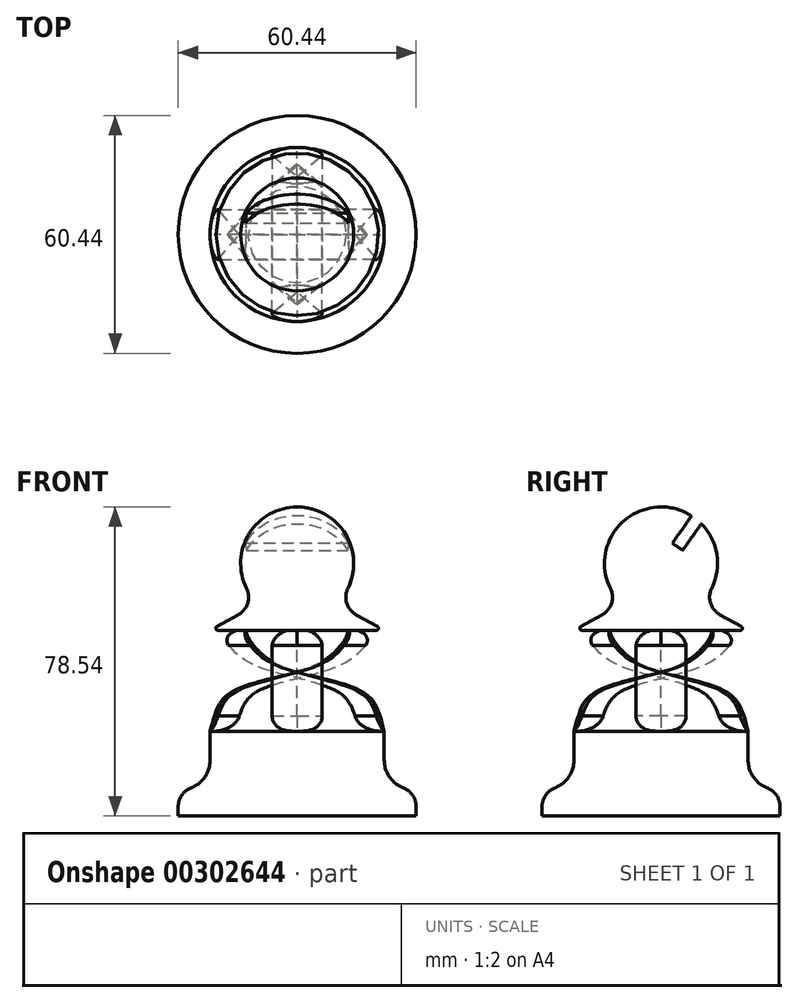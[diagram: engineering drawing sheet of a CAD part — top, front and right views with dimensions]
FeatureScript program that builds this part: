
annotation { "Feature Type Name" : "Feature", "Feature Type Description" : "" }
export const myFeature = defineFeature(function(context is Context, id is Id, definition is map)
    precondition{}
    {
        {
            var Q0;
            Q0=qCreatedBy(makeId("Front.planeOp"),FACE);
            var sketch = newSketch(context, id + "F0", { "sketchPlane" : qUnion([Q0])});
            skLineSegment(sketch, "E0", {"start": v(0, 0) * mm, "end": v(-30.22, 0) * mm});
            skLineSegment(sketch, "E1", {"start": v(-30.22, 0) * mm, "end": v(-30.22, 6.62) * mm});
            skLineSegment(sketch, "E2", {"start": v(-30.22, 6.62) * mm, "end": v(-22.11, 6.62) * mm});
            skLineSegment(sketch, "E3", {"start": v(-22.11, 6.62) * mm, "end": v(-22.11, 21.54) * mm});
            skLineSegment(sketch, "E4", {"start": v(-22.11, 21.54) * mm, "end": v(0, 21.54) * mm});
            skLineSegment(sketch, "E5", {"start": v(0, 21.54) * mm, "end": v(0, 0) * mm});
            skLineSegment(sketch, "E6", {"start": v(0, 47.18) * mm, "end": v(-22.11, 47.18) * mm});
            skLineSegment(sketch, "E7", {"start": v(-22.11, 47.18) * mm, "end": v(-10, 53.9) * mm});
            skArc(sketch, "E8", {"start": v(0, 78.54) * mm, "mid": v(-13.3, 69.58) * mm, "end": v(-10, 53.9) * mm});
            skLineSegment(sketch, "E9", {"start": v(0, 47.18) * mm, "end": v(0, 78.54) * mm});
            skSolve(sketch);
        }
        {
            var Q0;
            Q0=qSketchRegion(id+"F0",true);
            var Q1;
            Q1=sQuery(id+"F0.wireOp",EDGE,"E9");
            revolve(context, id + "F1", {"entities" : qUnion([Q0]), "axis" : qUnion([Q1]), "revolveType" : RevolveType.FULL});
        }
        {
            var Q0;
            Q0=makeQuery(id+"F1.opRevolve","SWEPT_FACE",FACE,{"disambiguationData":[OSD([sQuery(id+"F0.wireOp",EDGE,"E4")])]});
            var sketch = newSketch(context, id + "F2", { "sketchPlane" : qUnion([Q0])});
            skArc(sketch, "E10.0", {"start": v(-6.35, -21.18) * mm, "mid": v(0, -22.11) * mm, "end": v(6.35, -21.18) * mm});
            skLineSegment(sketch, "E11", {"start": v(-6.35, -21.18) * mm, "end": v(0, -15.76) * mm});
            skLineSegment(sketch, "E12", {"start": v(0, -15.76) * mm, "end": v(6.35, -21.18) * mm});
            skSolve(sketch);
        }
        {
            var Q0;
            Q0=makeQuery(id+"F1.opRevolve","SWEPT_EDGE",EDGE,{"disambiguationData":[OSD([sQuery(id+"F0.wireOp",EDGE,"E2"),sQuery(id+"F0.wireOp",EDGE,"E3")])]});
            fillet(context, id + "F3", {"entities" : qUnion([Q0]), "radius" : 7.62 * mm, "tangentPropagation" : true, "allowEdgeOverflow" : false});
        }
        {
            var Q0;
            Q0=makeQuery(id+"F1.opRevolve","SWEPT_EDGE",EDGE,{"disambiguationData":[OSD([sQuery(id+"F0.wireOp",EDGE,"E1"),sQuery(id+"F0.wireOp",EDGE,"E2")])]});
            fillet(context, id + "F4", {"entities" : qUnion([Q0]), "radius" : 5.08 * mm, "tangentPropagation" : true, "allowEdgeOverflow" : false});
        }
        {
            var Q0;
            Q0=makeQuery(id+"F1.opRevolve","SWEPT_EDGE",EDGE,{"disambiguationData":[OSD([sQuery(id+"F0.wireOp",EDGE,"E7"),sQuery(id+"F0.wireOp",EDGE,"E8")])]});
            fillet(context, id + "F5", {"entities" : qUnion([Q0]), "radius" : 5.08 * mm, "tangentPropagation" : true, "allowEdgeOverflow" : false});
        }
        {
            var Q0;
            Q0=qCreatedBy(makeId("Right.planeOp"),FACE);
            var sketch = newSketch(context, id + "F6", { "sketchPlane" : qUnion([Q0])});
            skFitSpline(sketch, "E13", {"points": [v(-15.76, 21.54) * mm, v(-12.86, 29.3) * mm, v(-7.35, 32.87) * mm, v(0, 35.04) * mm, v(6.19, 36.7) * mm, v(14.66, 40.62) * mm, v(19.27, 47.18) * mm], "startDerivative": vector(10.42, 41.06) * mm, "endDerivative": vector(-2.91, 25.6) * mm});
            skSolve(sketch);
        }
        {
            var Q0;
            Q0=makeQuery(id+"F2.imprint","IMPRINT",FACE,{"disambiguationData":[TD([[makeQuery(id+"F2.imprint","IMPRINT",EDGE,{"derivedFrom":sQuery(id+"F2.wireOp",EDGE,"E10.0")}),-1.0]])]});
            var Q1;
            Q1=sQuery(id+"F6.wireOp",EDGE,"E13");
            sweep(context, id + "F7", {"profiles" : qUnion([Q0]), "path" : qUnion([Q1]), "keepProfileOrientation" : true});
        }
        {
            var Q0;
            Q0=makeQuery(id+"F7.opSweep","SWEPT_BODY",BODY,{"disambiguationData":[OSD([sQuery(id+"F2.wireOp",EDGE,"E10.0"),sQuery(id+"F2.wireOp",EDGE,"E11"),sQuery(id+"F2.wireOp",EDGE,"E12"),sQuery(id+"F6.wireOp",EDGE,"E13")])]});
            var Q1;
            Q1=makeQuery(id+"F1.opRevolve","SWEPT_EDGE",EDGE,{"disambiguationData":[OSD([sQuery(id+"F0.wireOp",EDGE,"E3"),sQuery(id+"F0.wireOp",EDGE,"E4")])]});
            circularPattern(context, id + "F8", {"entities" : qUnion([Q0]), "axis" : qUnion([Q1]), "angle" : 360 * degree, "instanceCount" : 4, "equalSpace" : true});
        }
        {
            var Q0;
            Q0=makeQuery(id+"F1.opRevolve","SWEPT_EDGE",EDGE,{"disambiguationData":[OSD([sQuery(id+"F0.wireOp",EDGE,"E6"),sQuery(id+"F0.wireOp",EDGE,"E7")])]});
            fillet(context, id + "F9", {"entities" : qUnion([Q0]), "radius" : 0.5 * mm, "tangentPropagation" : true, "allowEdgeOverflow" : false});
        }
        {
            var Q0;
            Q0=makeQuery(id+"F8.opPattern","COPY",EDGE,{"derivedFrom":makeQuery(id+"F7.opSweep","CAP_EDGE",EDGE,{"disambiguationData":[OSD([sQuery(id+"F2.wireOp",EDGE,"E12"),sQuery(id+"F6.wireOp",VERTEX,"E13.start")])],"isStart":true}),"instanceName":"3"});
            var Q1;
            Q1=makeQuery(id+"F8.opPattern","COPY",EDGE,{"derivedFrom":makeQuery(id+"F7.opSweep","CAP_EDGE",EDGE,{"disambiguationData":[OSD([sQuery(id+"F2.wireOp",EDGE,"E11"),sQuery(id+"F6.wireOp",VERTEX,"E13.start")])],"isStart":true}),"instanceName":"2"});
            var Q2;
            Q2=makeQuery(id+"F8.opPattern","COPY",EDGE,{"derivedFrom":makeQuery(id+"F7.opSweep","CAP_EDGE",EDGE,{"disambiguationData":[OSD([sQuery(id+"F2.wireOp",EDGE,"E12"),sQuery(id+"F6.wireOp",VERTEX,"E13.start")])],"isStart":true}),"instanceName":"2"});
            var Q3;
            Q3=makeQuery(id+"F8.opPattern","COPY",EDGE,{"derivedFrom":makeQuery(id+"F7.opSweep","CAP_EDGE",EDGE,{"disambiguationData":[OSD([sQuery(id+"F2.wireOp",EDGE,"E11"),sQuery(id+"F6.wireOp",VERTEX,"E13.start")])],"isStart":true}),"instanceName":"1"});
            var Q4;
            Q4=makeQuery(id+"F8.opPattern","COPY",EDGE,{"derivedFrom":makeQuery(id+"F7.opSweep","CAP_EDGE",EDGE,{"disambiguationData":[OSD([sQuery(id+"F2.wireOp",EDGE,"E12"),sQuery(id+"F6.wireOp",VERTEX,"E13.start")])],"isStart":true}),"instanceName":"1"});
            var Q5;
            Q5=makeQuery(id+"F7.opSweep","CAP_EDGE",EDGE,{"disambiguationData":[OSD([sQuery(id+"F2.wireOp",EDGE,"E11"),sQuery(id+"F6.wireOp",VERTEX,"E13.start")])],"isStart":true});
            var Q6;
            Q6=makeQuery(id+"F7.opSweep","CAP_EDGE",EDGE,{"disambiguationData":[OSD([sQuery(id+"F2.wireOp",EDGE,"E12"),sQuery(id+"F6.wireOp",VERTEX,"E13.start")])],"isStart":true});
            var Q7;
            Q7=makeQuery(id+"F8.opPattern","COPY",EDGE,{"derivedFrom":makeQuery(id+"F7.opSweep","CAP_EDGE",EDGE,{"disambiguationData":[OSD([sQuery(id+"F2.wireOp",EDGE,"E11"),sQuery(id+"F6.wireOp",VERTEX,"E13.start")])],"isStart":true}),"instanceName":"3"});
            fillet(context, id + "F10", {"entities" : qUnion([Q0, Q1, Q2, Q3, Q4, Q5, Q6, Q7]), "radius" : 5.08 * mm, "tangentPropagation" : true, "allowEdgeOverflow" : false});
        }
        {
            var Q0;
            Q0=makeQuery(id+"F7.opSweep","CAP_EDGE",EDGE,{"disambiguationData":[OSD([sQuery(id+"F2.wireOp",EDGE,"E11"),sQuery(id+"F6.wireOp",VERTEX,"E13.end")])],"isStart":false});
            var Q1;
            Q1=makeQuery(id+"F7.opSweep","CAP_EDGE",EDGE,{"disambiguationData":[OSD([sQuery(id+"F2.wireOp",EDGE,"E12"),sQuery(id+"F6.wireOp",VERTEX,"E13.end")])],"isStart":false});
            var Q2;
            Q2=makeQuery(id+"F8.opPattern","COPY",EDGE,{"derivedFrom":makeQuery(id+"F7.opSweep","CAP_EDGE",EDGE,{"disambiguationData":[OSD([sQuery(id+"F2.wireOp",EDGE,"E12"),sQuery(id+"F6.wireOp",VERTEX,"E13.end")])],"isStart":false}),"instanceName":"3"});
            var Q3;
            Q3=makeQuery(id+"F8.opPattern","COPY",EDGE,{"derivedFrom":makeQuery(id+"F7.opSweep","CAP_EDGE",EDGE,{"disambiguationData":[OSD([sQuery(id+"F2.wireOp",EDGE,"E11"),sQuery(id+"F6.wireOp",VERTEX,"E13.end")])],"isStart":false}),"instanceName":"3"});
            var Q4;
            Q4=makeQuery(id+"F8.opPattern","COPY",EDGE,{"derivedFrom":makeQuery(id+"F7.opSweep","CAP_EDGE",EDGE,{"disambiguationData":[OSD([sQuery(id+"F2.wireOp",EDGE,"E12"),sQuery(id+"F6.wireOp",VERTEX,"E13.end")])],"isStart":false}),"instanceName":"2"});
            var Q5;
            Q5=makeQuery(id+"F8.opPattern","COPY",EDGE,{"derivedFrom":makeQuery(id+"F7.opSweep","CAP_EDGE",EDGE,{"disambiguationData":[OSD([sQuery(id+"F2.wireOp",EDGE,"E11"),sQuery(id+"F6.wireOp",VERTEX,"E13.end")])],"isStart":false}),"instanceName":"2"});
            var Q6;
            Q6=makeQuery(id+"F8.opPattern","COPY",EDGE,{"derivedFrom":makeQuery(id+"F7.opSweep","CAP_EDGE",EDGE,{"disambiguationData":[OSD([sQuery(id+"F2.wireOp",EDGE,"E12"),sQuery(id+"F6.wireOp",VERTEX,"E13.end")])],"isStart":false}),"instanceName":"1"});
            var Q7;
            Q7=makeQuery(id+"F8.opPattern","COPY",EDGE,{"derivedFrom":makeQuery(id+"F7.opSweep","CAP_EDGE",EDGE,{"disambiguationData":[OSD([sQuery(id+"F2.wireOp",EDGE,"E11"),sQuery(id+"F6.wireOp",VERTEX,"E13.end")])],"isStart":false}),"instanceName":"1"});
            fillet(context, id + "F11", {"entities" : qUnion([Q0, Q1, Q2, Q3, Q4, Q5, Q6, Q7]), "radius" : 2.54 * mm, "tangentPropagation" : true, "allowEdgeOverflow" : false});
        }
        {
            var Q0;
            Q0=qCreatedBy(makeId("Right.planeOp"),FACE);
            var sketch = newSketch(context, id + "F12", { "sketchPlane" : qUnion([Q0])});
            skLineSegment(sketch, "E14", {"start": v(10.59, 80.32) * mm, "end": v(2.88, 69.32) * mm});
            skLineSegment(sketch, "E15", {"start": v(2.88, 69.32) * mm, "end": v(5.49, 67.5) * mm});
            skLineSegment(sketch, "E16", {"start": v(5.49, 67.5) * mm, "end": v(13.23, 78.55) * mm});
            skLineSegment(sketch, "E17", {"start": v(13.23, 78.55) * mm, "end": v(10.59, 80.32) * mm});
            skSolve(sketch);
        }
        {
            var Q0;
            Q0 = qSketchRegion(id + "F12", true);
            extrude(context, id + "F13", {"entities" : qUnion([Q0]), "operationType" : NewBodyOperationType.REMOVE, "endBound" : BoundingType.SYMMETRIC, "oppositeDirection" : true, "depth" : 93.98 * mm});
        }
    });
